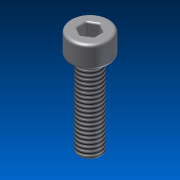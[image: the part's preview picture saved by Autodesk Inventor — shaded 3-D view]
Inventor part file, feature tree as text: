
AUTODESK INVENTOR PART (.ipt)
format: ipt  version: 2013 (Build 170138000, 138)  size: 152,576 bytes
history: native  units: mm
features: extrude x3, sketch x3, fillet x2, other x1, thread x1
ambient origin geometry x1: Origin
feature tree (10):
  other  "ソリッド1"
  extrude  "押し出し1"  Depth=7.0mm
  extrude  "押し出し2"  Depth=4.0mm TaperAngle=0.0deg
  extrude  "押し出し3"  Depth=4.0mm
  thread  "ねじ1"
  fillet  "フィレット1"  Radius=15.0mm
  fillet  "フィレット2"  Radius=1.5mm
  sketch  "スケッチ1"
  sketch  "スケッチ2"
  sketch  "スケッチ3"
